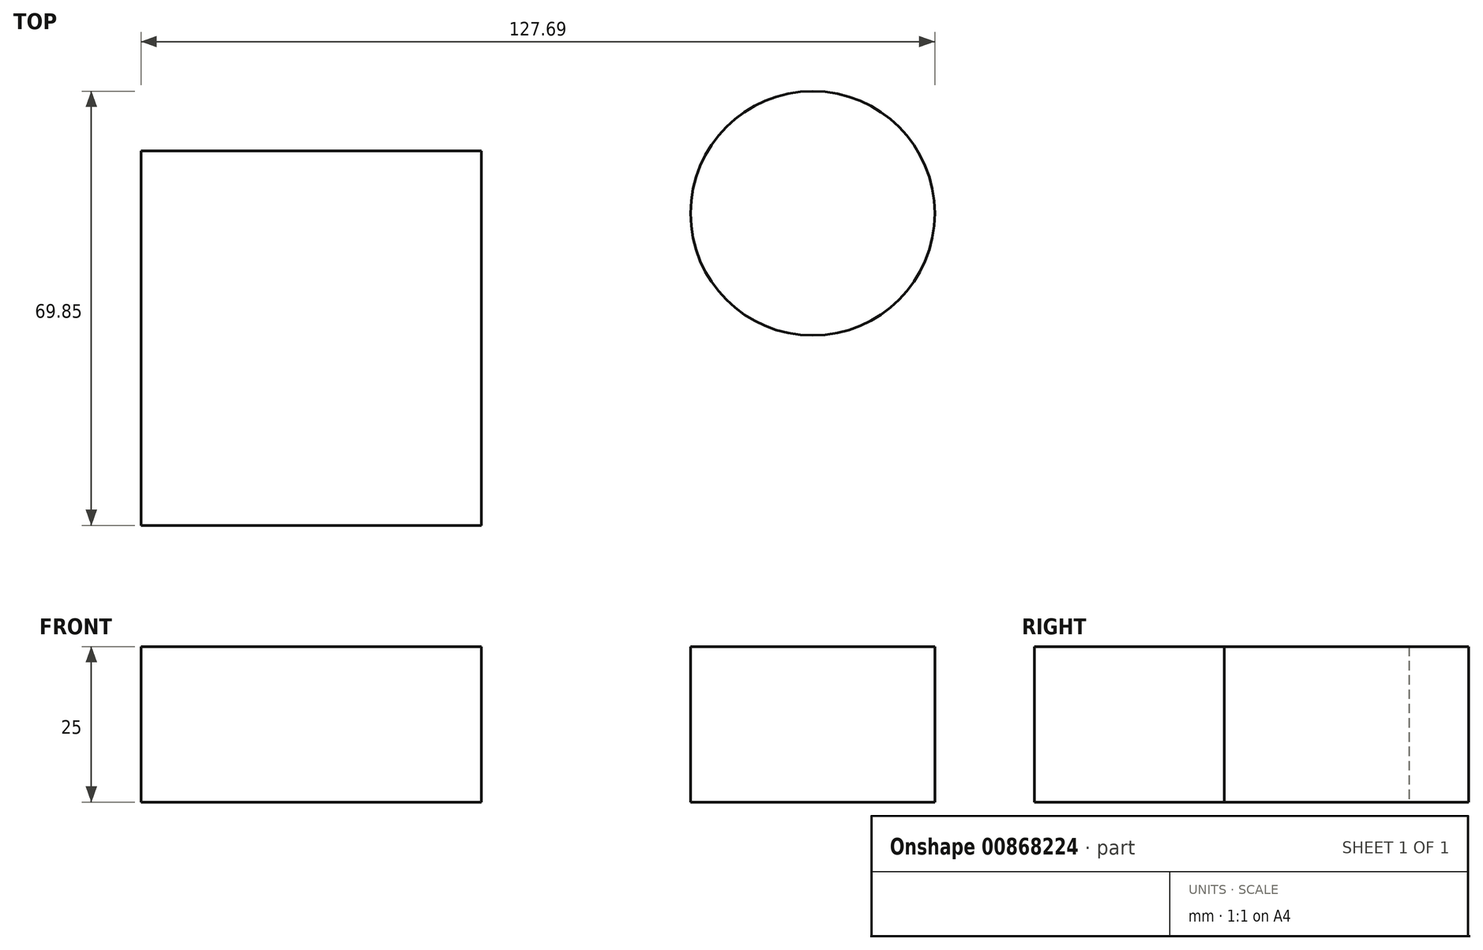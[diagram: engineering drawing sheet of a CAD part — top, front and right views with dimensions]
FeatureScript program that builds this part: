
annotation { "Feature Type Name" : "Feature", "Feature Type Description" : "" }
export const myFeature = defineFeature(function(context is Context, id is Id, definition is map)
    precondition{}
    {
        {
            var Q0;
            Q0=qCreatedBy(makeId("Front.planeOp"),FACE);
            var sketch = newSketch(context, id + "F0", { "sketchPlane" : qUnion([Q0])});
            skLineSegment(sketch, "E0", {"start": v(0, 0) * mm, "end": v(0, 90.84) * mm});
            skSolve(sketch);
        }
        {
            var Q0;
            Q0=qCreatedBy(makeId("Top.planeOp"),FACE);
            cPlane(context, id + "F1", {"entities" : qUnion([Q0]), "cplaneType" : CPlaneType.OFFSET, "offset" : 25 * mm, "width" : 150 * mm, "height" : 150 * mm});
        }
        {
            var Q0;
            Q0=qCreatedBy(id+"F1.planeOp",FACE);
            var sketch = newSketch(context, id + "F2", { "sketchPlane" : qUnion([Q0])});
            skCircle(sketch, "E1", {"center": v(0, 0) * mm, "radius": 19.64 * mm});
            skLineSegment(sketch, "E2.bottom", {"start": v(-108.05, 10.06) * mm, "end": v(-53.28, 10.06) * mm});
            skLineSegment(sketch, "E2.top", {"start": v(-108.05, -50.2) * mm, "end": v(-53.28, -50.2) * mm});
            skLineSegment(sketch, "E2.left", {"start": v(-108.05, 10.06) * mm, "end": v(-108.05, -50.2) * mm});
            skLineSegment(sketch, "E2.right", {"start": v(-53.28, 10.06) * mm, "end": v(-53.28, -50.2) * mm});
            skSolve(sketch);
        }
        {
            var Q0;
            Q0 = qSketchRegion(id + "F2", true);
            extrude(context, id + "F3", {"entities" : qUnion([Q0]), "depth" : 25 * mm, "offsetDistance" : 25 * mm});
        }
    });
